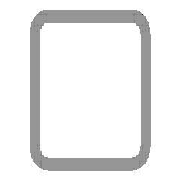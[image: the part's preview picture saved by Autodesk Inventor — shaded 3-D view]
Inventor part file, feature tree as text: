
AUTODESK INVENTOR PART (.ipt)
format: ipt  version: 2025 (Build 290162010, 162A)  size: 134,656 bytes
history: native  units: mm (DEFAULTED — no unit token found)
features: other x4, sketch x1, plane x1
ambient origin geometry x8: Origin, YZ Plane, XZ Plane, XY Plane, X Axis, Y Axis, Z Axis, Center Point
bodies: Solid1 (feature_tree), Body (feature_tree)
feature tree (6):
  parser-record x1  (decoder bookkeeping rows leaked as tree rows — omitted from the tree; the rows remain in map.json)
  other  "Driven Length"
  other  "Start Plane"
  other  "End Plane"
  sketch  "Sketch3"  dims[d3=1400.0mm d4=0.0mm d7=4.5mm d10=80.0mm d11=80.0mm d12=3.0mm d13=-0.0mm d14=1400.0mm d15=40.0mm d16=40.0mm d17=90.0deg d18=1400.0mm]
  plane  "Work Plane3"
